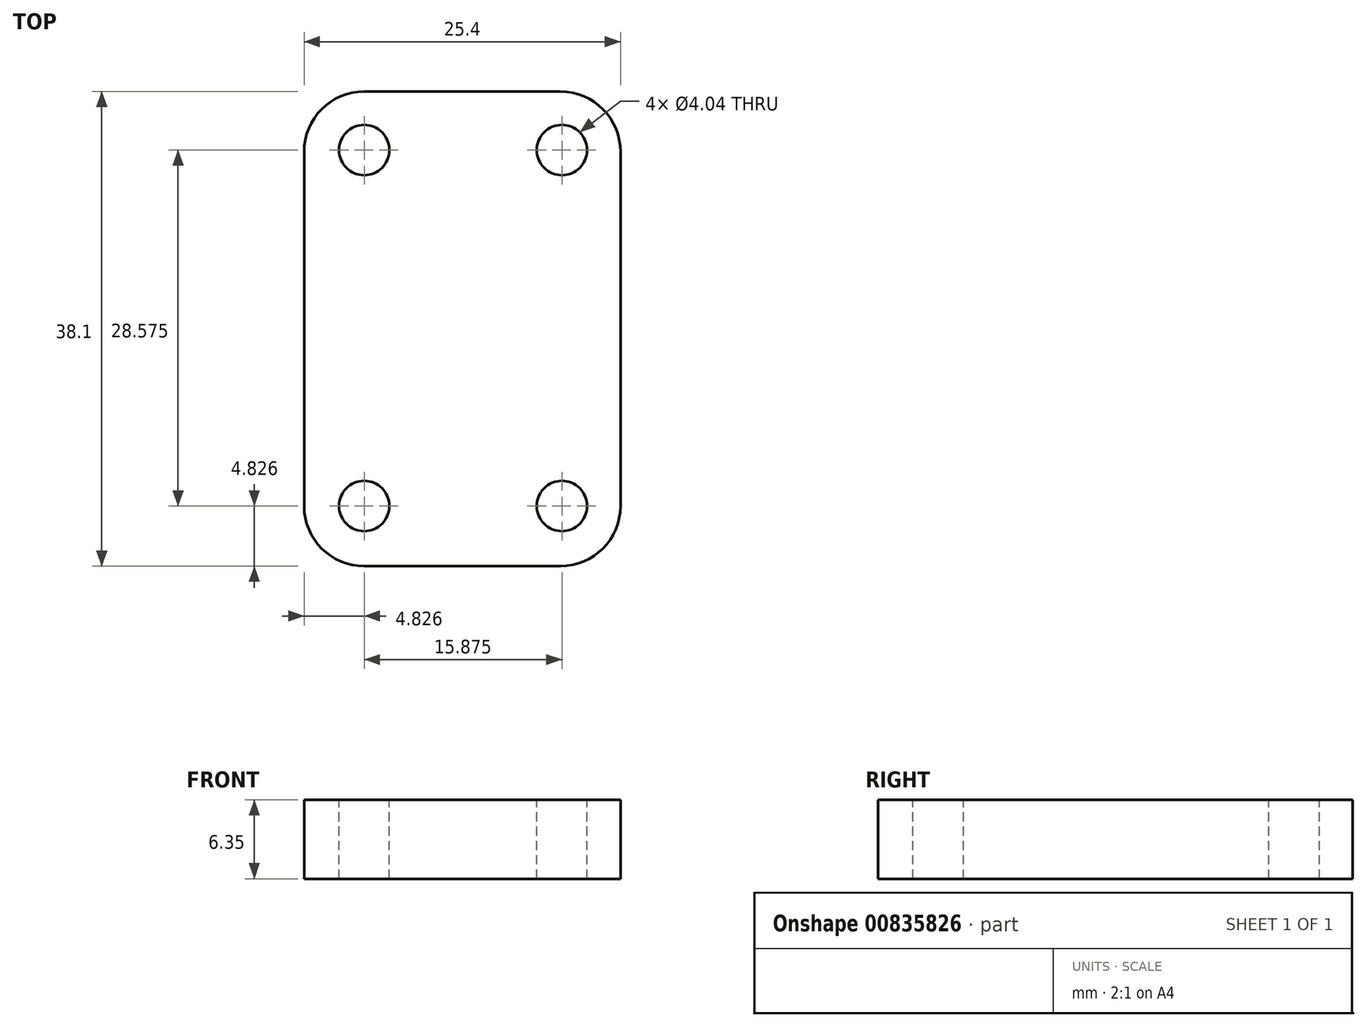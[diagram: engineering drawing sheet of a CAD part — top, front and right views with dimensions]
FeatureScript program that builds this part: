
annotation { "Feature Type Name" : "Feature", "Feature Type Description" : "" }
export const myFeature = defineFeature(function(context is Context, id is Id, definition is map)
    precondition{}
    {
        {
            var Q0;
            Q0=qCreatedBy(makeId("Top.planeOp"),FACE);
            var sketch = newSketch(context, id + "F0", { "sketchPlane" : qUnion([Q0])});
            skLineSegment(sketch, "E0.bottom", {"start": v(12.7, 19.05) * mm, "end": v(-12.7, 19.05) * mm});
            skLineSegment(sketch, "E0.top", {"start": v(12.7, -19.05) * mm, "end": v(-12.7, -19.05) * mm});
            skLineSegment(sketch, "E0.left", {"start": v(12.7, 19.05) * mm, "end": v(12.7, -19.05) * mm});
            skLineSegment(sketch, "E0.right", {"start": v(-12.7, 19.05) * mm, "end": v(-12.7, -19.05) * mm});
            skPoint(sketch, "E0.middle", {"position": v(0, 0) * mm});
            skSolve(sketch);
        }
        {
            var Q0;
            Q0 = qSketchRegion(id + "F0", true);
            extrude(context, id + "F1", {"entities" : qUnion([Q0]), "depth" : 6.35 * mm, "offsetDistance" : 25.4 * mm});
        }
        {
            var Q0;
            Q0=makeQuery(id+"F1.opExtrude","CAP_FACE",FACE,{"disambiguationData":[OSD([sQuery(id+"F0.wireOp",EDGE,"E0.bottom"),sQuery(id+"F0.wireOp",EDGE,"E0.top"),sQuery(id+"F0.wireOp",EDGE,"E0.left"),sQuery(id+"F0.wireOp",EDGE,"E0.right")])],"isStart":false});
            var sketch = newSketch(context, id + "F2", { "sketchPlane" : qUnion([Q0])});
            skPoint(sketch, "E1", {"position": v(-7.87, 14.35) * mm});
            skPoint(sketch, "E2", {"position": v(8, 14.35) * mm});
            skPoint(sketch, "E3", {"position": v(8, -14.22) * mm});
            skPoint(sketch, "E4", {"position": v(-7.87, -14.22) * mm});
            skSolve(sketch);
        }
        {
            var Q0;
            Q0=sQuery(id+"F2.wireOp",VERTEX,"E1");
            var Q1;
            Q1=sQuery(id+"F2.wireOp",VERTEX,"E2");
            var Q2;
            Q2=sQuery(id+"F2.wireOp",VERTEX,"E3");
            var Q3;
            Q3=sQuery(id+"F2.wireOp",VERTEX,"E4");
            var Q4;
            Q4=makeQuery(id+"F1.opExtrude","SWEPT_BODY",BODY,{"disambiguationData":[OSD([sQuery(id+"F0.wireOp",EDGE,"E0.bottom"),sQuery(id+"F0.wireOp",EDGE,"E0.top"),sQuery(id+"F0.wireOp",EDGE,"E0.left"),sQuery(id+"F0.wireOp",EDGE,"E0.right")])]});
            hole(context, id + "F3", {"style" : HoleStyle.SIMPLE, "endStyle" : HoleEndStyle.THROUGH, "holeDiameter" : 4.04 * mm, "majorDiameter" : 6.35 * mm, "isTappedThrough" : true, "tappedDepth" : 12.7 * mm, "tapClearance" : 3, "locations" : qUnion([Q0, Q1, Q2, Q3]), "scope" : qUnion([Q4])});
        }
        {
            var Q0;
            Q0=makeQuery(id+"F1.opExtrude","SWEPT_EDGE",EDGE,{"disambiguationData":[OSD([sQuery(id+"F0.wireOp",EDGE,"E0.top"),sQuery(id+"F0.wireOp",EDGE,"E0.right")])]});
            var Q1;
            Q1=makeQuery(id+"F1.opExtrude","SWEPT_EDGE",EDGE,{"disambiguationData":[OSD([sQuery(id+"F0.wireOp",EDGE,"E0.top"),sQuery(id+"F0.wireOp",EDGE,"E0.left")])]});
            var Q2;
            Q2=makeQuery(id+"F1.opExtrude","SWEPT_EDGE",EDGE,{"disambiguationData":[OSD([sQuery(id+"F0.wireOp",EDGE,"E0.bottom"),sQuery(id+"F0.wireOp",EDGE,"E0.left")])]});
            var Q3;
            Q3=makeQuery(id+"F1.opExtrude","SWEPT_EDGE",EDGE,{"disambiguationData":[OSD([sQuery(id+"F0.wireOp",EDGE,"E0.bottom"),sQuery(id+"F0.wireOp",EDGE,"E0.right")])]});
            fillet(context, id + "F4", {"entities" : qUnion([Q0, Q1, Q2, Q3]), "radius" : 4.83 * mm, "tangentPropagation" : true, "allowEdgeOverflow" : false});
        }
    });
